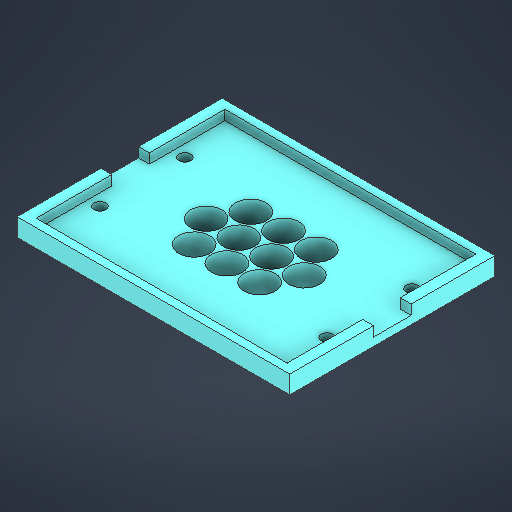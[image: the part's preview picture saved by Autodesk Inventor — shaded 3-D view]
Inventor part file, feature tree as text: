
AUTODESK INVENTOR PART (.ipt)
format: ipt  version: 2025.2 (Build 292293000, 293)  size: 674,816 bytes
history: native  units: mm
features: extrude x5, sketch x5, projected_geometry x4
ambient origin geometry x8: Origin, YZ Plane, XZ Plane, XY Plane, X Axis, Y Axis, Z Axis, Center Point
bodies: Solid1 (feature_tree)
feature tree (14):
  extrude  "Extrusion1"  Depth=19.0mm
  sketch  "Sketch4"  dims[d4=19.0mm d6=19.0mm]
  extrude  "Extrusion7"  Depth=19.0mm
  sketch  "Sketch5"  dims[d8=19.0mm d10=19.0mm]
  extrude  "Extrusion8"  Depth=19.0mm
  extrude  "Extrusion6"  Depth=19.0mm
  extrude  "Extrusion9"  Depth=15.0mm TaperAngle=0.0deg
  sketch  "Sketch1"  dims[d0=19.0mm d2=19.0mm]
  projected_geometry  "Projected Loop1"
  sketch  "Sketch6"  dims[d11=19.0mm d13=19.0mm]
  projected_geometry  "Projected Loop4"
  sketch  "Sketch7"  dims[d14=19.0mm d16=20.0mm d17=20.0mm d18=20.0mm d19=20.0mm d20=20.0mm d21=20.0mm d22=20.0mm d23=20.0mm d24=15.0mm d25=0.0mm d53=19.0mm d91=1.0mm d104=153.4mm d123=7.23mm d124=7.23mm d125=7.23mm d126=0.0mm d127=0.0mm d140=7.23mm d144=21.0mm d145=21.0mm d146=21.0mm d147=21.0mm d148=21.0mm d149=21.0mm d150=21.0mm d151=21.0mm d152=21.0mm d153=21.0mm d154=23.0mm d155=23.0mm d156=23.0mm d157=23.0mm d158=23.0mm d159=23.0mm d160=23.0mm d161=23.0mm d162=23.0mm d163=23.0mm d164=115.4mm d165=8.0mm d166=0.0mm d169=5.0mm d170=6.646447mm d171=166.692894mm d172=125.4mm d173=6.0mm d174=5.0mm d175=0.0mm d176=0.0mm d177=0.0mm d178=0.0mm d179=31.75mm d180=7.228mm d181=7.228mm d182=31.75mm d183=31.75mm d184=7.228mm d185=7.228mm d186=31.75mm]
  projected_geometry  "Projected Loop5"
  projected_geometry  "Projected Loop6"
